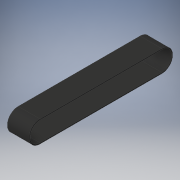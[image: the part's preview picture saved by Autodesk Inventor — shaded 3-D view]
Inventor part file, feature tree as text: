
AUTODESK INVENTOR PART (.ipt)
format: ipt  version: 2019 (Build 230136000, 136)  size: 115,200 bytes
history: native  units: mm
features: extrude x2, sketch x2, other x1
ambient origin geometry x8: Origin, YZ Plane, XZ Plane, XY Plane, X Axis, Y Axis, Z Axis, Center Point
bodies: Body1 (feature_tree)
feature tree (5):
  other  "ソリッド1"
  extrude  "押し出し1"  Depth=224.336mm
  extrude  "押し出し2"  Depth=224.336mm
  sketch  "スケッチ1"
  sketch  "スケッチ2"
